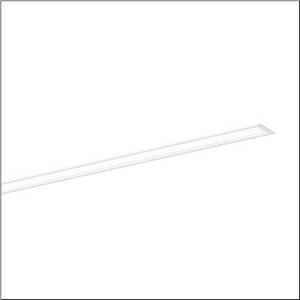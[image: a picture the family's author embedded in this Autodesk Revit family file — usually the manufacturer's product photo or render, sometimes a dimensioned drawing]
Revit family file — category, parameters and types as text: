
# Revit family: silica_21_51mx13tctaw
name_source: partatom
category: Lighting Fixtures
units: mm (PartAtom-declared; Revit-internal decimal feet)

## family parameters
Cut with Voids When Loaded = No
Host = Face
Light Source = No
Part Type = Normal
Room Calculation Point = No
Round Connector Dimension = Use Diameter
Shared = No

## types (1)
- --- (1 x LED, 8070 lm, 81.1 W, 6500K)
    Apparent Load = 81 VA
    CIE Flux Codes = 78 96 99 100 100
    Color Rendering = 80
    Color Temperature = 6500K
    Default Elevation = 1800 mm
    Description = Silica 21, office luminaire, primary optical cover: prismatic diffuser, of PMMA, CAT 2 (L<= 3000cd/m²), light emission: direct distribution, primary light characteristic: symmetric, installation type: recessed, LED, rated luminous flux: 8.070lm, luminous efficacy: 95lm/W, light colour: 8tw, colour temperature: 2700..6500K, control gear: DALI DT8, with terminal, 3+2-pole, max. 2.5mm², mains connection: 220..240V, AC, 50/60Hz, rated input power: 85.1W, luminaire housing, of aluminium, traffic white (RAL 9016), length: 3.028mm, width: 79mm, height: 53mm, protection rating (complete): IP20, insulation class (complete): insulation class I (protective earthing), certification: CE, ENEC, VDE, permissible operating ambient temperature: 0..+35°C, standard: EN 50419, packaging unit: 1 piece
    Height = 0 mm  [stored 0 ft]
    Lamp = 1 x LED
    Lamp Light Flux = 8070 lm
    Lamp Power = 81.1 W
    Lamp count = 1
    Length = 3027 mm
    Luminous efficacy = 100 lm/W
    Manufacturer = Siteco
    ModVariant = No
    Model = 51MX13TCTAW
    Mounting Place = Ceiling
    Mounting Type = Recessed
    Number of Poles = 1
    OnlyDefault = Yes
    Power Factor = 1
    Product Name = Silica 21
    Product group = office luminaire | ceiling recessed
    ProductGroupID = 400
    Protection Class = Protection class I
    Protection Degree = IP 20
    RLX_Detail_Level = 1
    RLX_Emergency_Light_Flux = 0 lm
    RLX_Emergency_Type = 0
    RLX_Emergency_Type_DB = No
    RlxData = <blob elided: 13037 chars, md5=4a2590fa>
    Socket = socket
    Standby Power = 0 W
    System Light Flux = 8070 lm
    System Power = 81 W
    Type Comments = individual setting
    Type Image = l_1335881.jpg
    URL = http://relux.com
    VarID = @adj_139337
    Voltage = 0 V
    Weight = 0.00 kg
    Width = 79 mm

note: [stored X ft] marks values corroborated as IEEE doubles in the binary element streams (Revit-internal decimal feet)

## geometry (parser evidence)
native form markers: Sweep x10
no freeform markers — native parametric forms only
